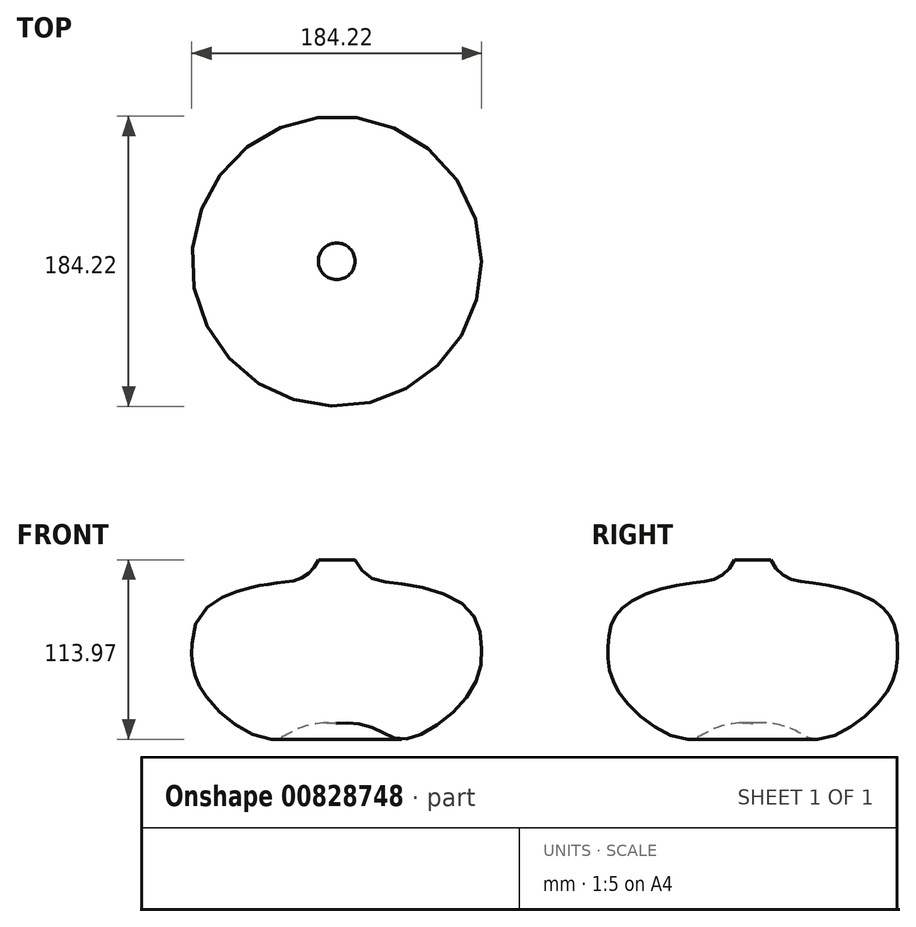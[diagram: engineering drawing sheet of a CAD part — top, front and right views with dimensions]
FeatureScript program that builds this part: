
annotation { "Feature Type Name" : "Feature", "Feature Type Description" : "" }
export const myFeature = defineFeature(function(context is Context, id is Id, definition is map)
    precondition{}
    {
        {
            var Q0;
            Q0=qCreatedBy(makeId("Front.planeOp"),FACE);
            var sketch = newSketch(context, id + "F0", { "sketchPlane" : qUnion([Q0])});
            skLineSegment(sketch, "E0", {"start": v(0, 0) * mm, "end": v(0, 217.32) * mm, "construction": true});
            skLineSegment(sketch, "E1", {"start": v(0, 0) * mm, "end": v(48.07, 0) * mm, "construction": true});
            skPoint(sketch, "E2", {"position": v(0, 10) * mm});
            skFitSpline(sketch, "E3", {"points": [v(0, 10) * mm, v(11.51, 10) * mm, v(27.1, 5.35) * mm, v(39.2, 0) * mm, v(60.59, 6.74) * mm, v(86.87, 33.03) * mm, v(91.99, 59.77) * mm, v(82.92, 83.26) * mm, v(44.34, 98.23) * mm, v(21.74, 102.5) * mm, v(11.64, 113.84) * mm], "startDerivative": vector(151.69, 10.69) * mm, "endDerivative": vector(-68.52, 166.25) * mm});
            skFitSpline(sketch, "E4", {"points": [v(11.64, 113.84) * mm, v(9.06, 119.6) * mm, v(11.64, 138.3) * mm, v(34.14, 150.04) * mm, v(59.85, 154.43) * mm, v(68.17, 160.7) * mm, v(71.95, 167.36) * mm], "startDerivative": vector(-27, 41.82) * mm, "endDerivative": vector(27.37, 56.54) * mm});
            skSolve(sketch);
        }
        {
            var Q0;
            Q0=sQuery(id+"F0.wireOp",EDGE,"E3");
            var Q1;
            Q1=sQuery(id+"F0.wireOp",EDGE,"E0");
            revolve(context, id + "F1", {"bodyType" : ToolBodyType.SURFACE, "surfaceOperationType" : NewSurfaceOperationType.NEW, "surfaceEntities" : qUnion([Q0]), "axis" : qUnion([Q1]), "revolveType" : RevolveType.FULL});
        }
    });
